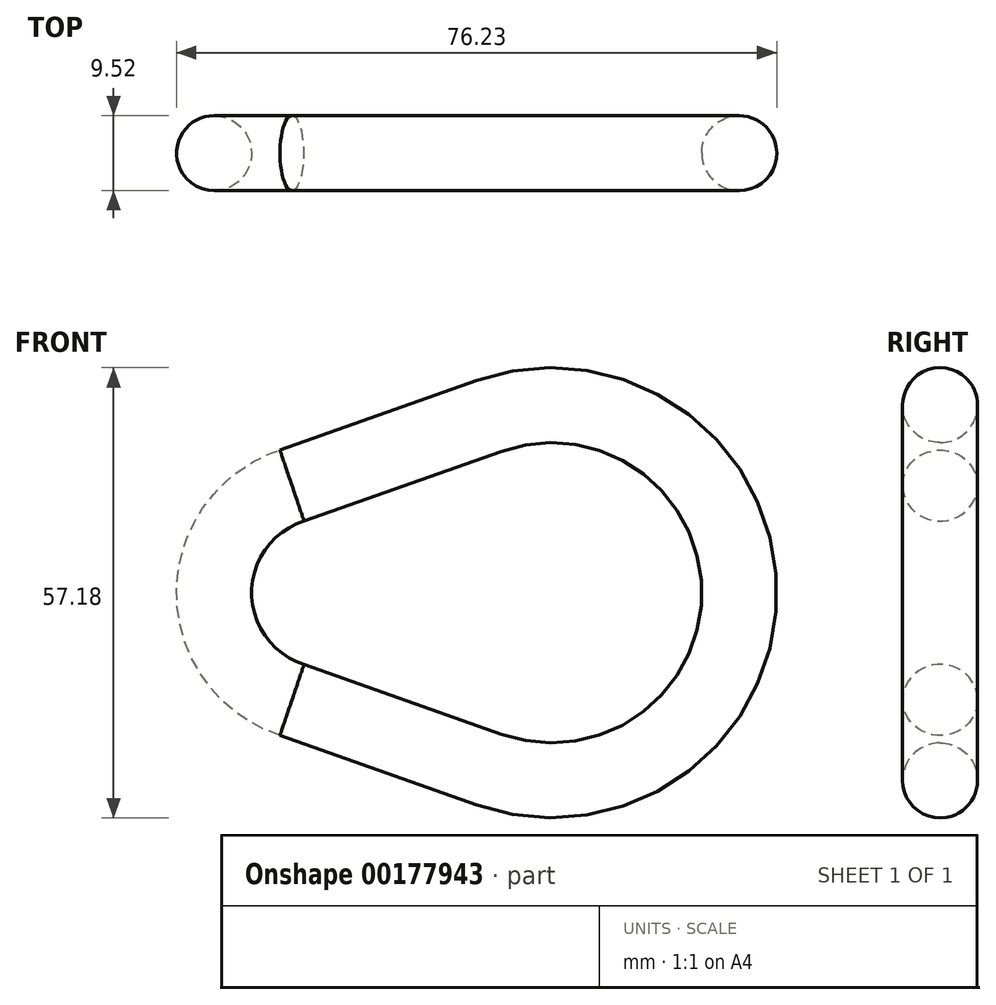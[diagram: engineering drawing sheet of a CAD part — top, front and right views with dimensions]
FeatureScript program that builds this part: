
annotation { "Feature Type Name" : "Feature", "Feature Type Description" : "" }
export const myFeature = defineFeature(function(context is Context, id is Id, definition is map)
    precondition{}
    {
        {
            var Q0;
            Q0=qCreatedBy(makeId("Front.planeOp"),FACE);
            var sketch = newSketch(context, id + "F0", { "sketchPlane" : qUnion([Q0])});
            skLineSegment(sketch, "E0.0", {"start": v(-32.97, 13.6) * mm, "end": v(-7.94, 22.45) * mm});
            skArc(sketch, "E1.0", {"start": v(-7.94, 22.45) * mm, "mid": v(23.81, 0) * mm, "end": v(-7.94, -22.45) * mm});
            skLineSegment(sketch, "E2.0", {"start": v(-32.97, -13.6) * mm, "end": v(-7.94, -22.45) * mm});
            skArc(sketch, "E3.0", {"start": v(-32.97, -13.6) * mm, "mid": v(-42.86, 0) * mm, "end": v(-32.97, 13.6) * mm});
            skSolve(sketch);
        }
        {
            var Q0;
            Q0=sQuery(id+"F0.wireOp",VERTEX,"E0.0.end");
            var Q1;
            Q1=sQuery(id+"F0.wireOp",EDGE,"E0.0");
            cPlane(context, id + "F1", {"entities" : qUnion([Q0, Q1]), "cplaneType" : CPlaneType.LINE_POINT, "offset" : 25.4 * mm, "width" : 152.4 * mm, "height" : 152.4 * mm});
        }
        {
            var Q0;
            Q0=qCreatedBy(id+"F1.planeOp",FACE);
            var sketch = newSketch(context, id + "F2", { "sketchPlane" : qUnion([Q0])});
            skCircle(sketch, "E4", {"center": v(0, 23.83) * mm, "radius": 4.76 * mm});
            skSolve(sketch);
        }
        {
            var Q0;
            Q0=makeQuery(id+"F2.imprint","IMPRINT",FACE,{"disambiguationData":[TD([[makeQuery(id+"F2.imprint","IMPRINT",EDGE,{"derivedFrom":sQuery(id+"F2.wireOp",EDGE,"E4")}),1.0]])]});
            var Q1;
            Q1=sQuery(id+"F0.wireOp",EDGE,"E0.0");
            var Q2;
            Q2=sQuery(id+"F0.wireOp",EDGE,"E3.0");
            var Q3;
            Q3=sQuery(id+"F0.wireOp",EDGE,"E2.0");
            var Q4;
            Q4=sQuery(id+"F0.wireOp",EDGE,"E1.0");
            sweep(context, id + "F3", {"profiles" : qUnion([Q0]), "path" : qUnion([Q1, Q2, Q3, Q4])});
        }
    });
